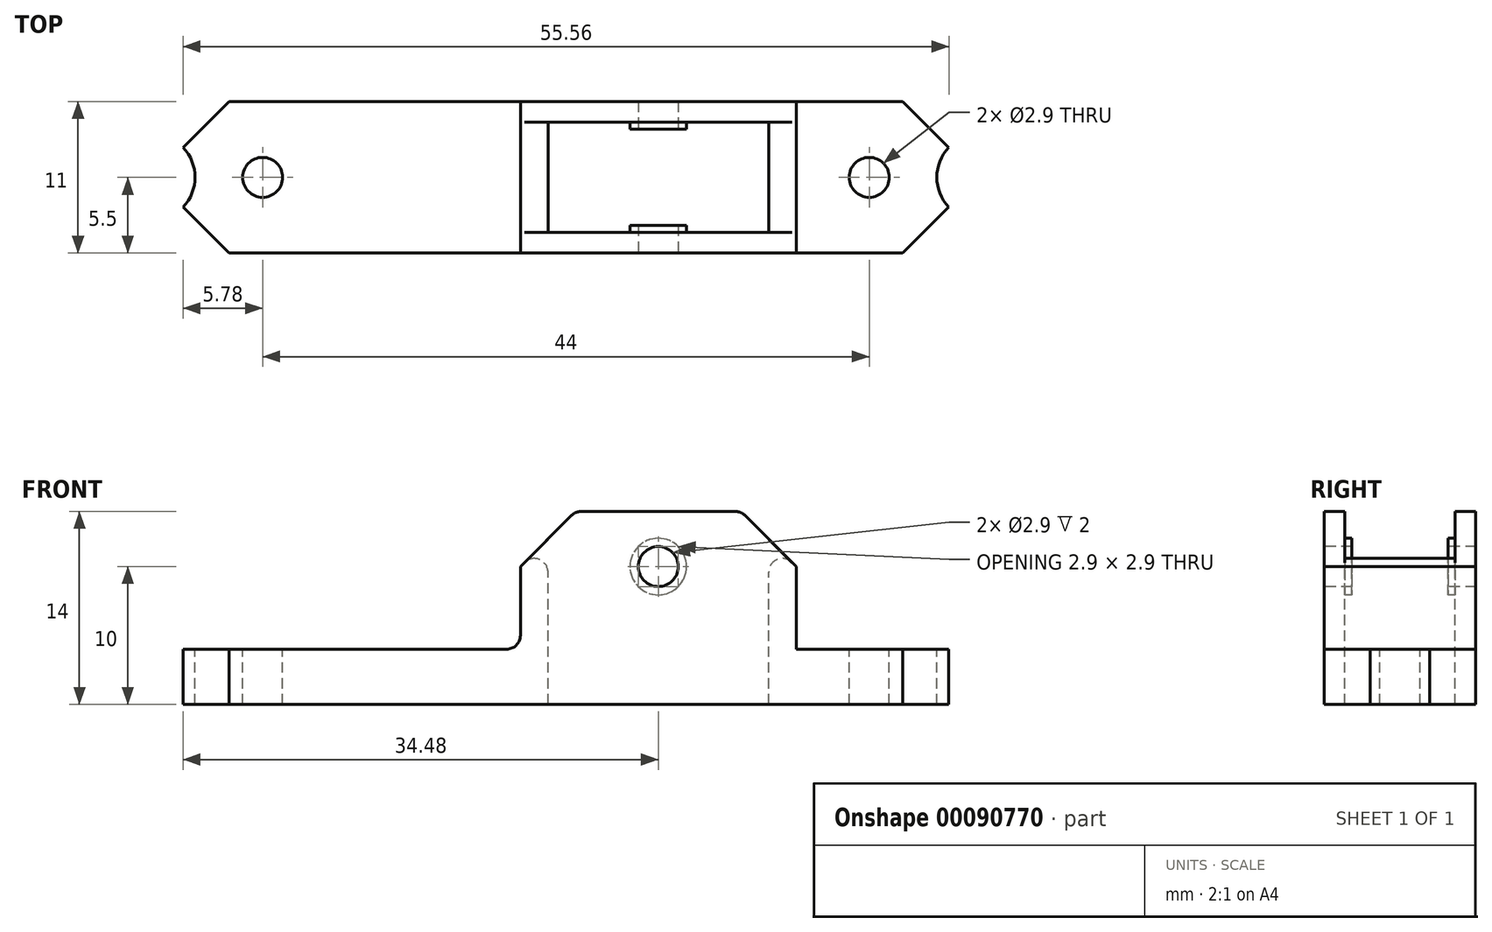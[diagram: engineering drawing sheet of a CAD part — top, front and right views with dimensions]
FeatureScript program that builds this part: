
annotation { "Feature Type Name" : "Feature", "Feature Type Description" : "" }
export const myFeature = defineFeature(function(context is Context, id is Id, definition is map)
    precondition{}
    {
        {
            var Q0;
            Q0=qCreatedBy(makeId("Top.planeOp"),FACE);
            var sketch = newSketch(context, id + "F0", { "sketchPlane" : qUnion([Q0])});
            skCircle(sketch, "E0", {"center": v(-30, 0) * mm, "radius": 3.1 * mm});
            skCircle(sketch, "E1", {"center": v(30, 0) * mm, "radius": 3.1 * mm});
            skLineSegment(sketch, "E2.bottom", {"start": v(-28.44, 5.5) * mm, "end": v(28.44, 5.5) * mm});
            skLineSegment(sketch, "E2.top", {"start": v(-28.44, -5.5) * mm, "end": v(28.44, -5.5) * mm});
            skLineSegment(sketch, "E2.left", {"start": v(-28.44, 5.5) * mm, "end": v(-28.44, -5.5) * mm});
            skLineSegment(sketch, "E2.right", {"start": v(28.44, 5.5) * mm, "end": v(28.44, -5.5) * mm});
            skPoint(sketch, "E2.middle", {"position": v(0, 0) * mm});
            skLineSegment(sketch, "E3.bottom", {"start": v(-1.3, 4) * mm, "end": v(14.7, 4) * mm});
            skLineSegment(sketch, "E3.top", {"start": v(-1.3, -4) * mm, "end": v(14.7, -4) * mm});
            skLineSegment(sketch, "E3.left", {"start": v(-1.3, 4) * mm, "end": v(-1.3, -4) * mm});
            skLineSegment(sketch, "E3.right", {"start": v(14.7, 4) * mm, "end": v(14.7, -4) * mm});
            skPoint(sketch, "E3.middle", {"position": v(6.7, 0) * mm});
            skLineSegment(sketch, "E4", {"start": v(-3.3, -5.5) * mm, "end": v(-3.3, 5.5) * mm});
            skLineSegment(sketch, "E5", {"start": v(16.7, -5.5) * mm, "end": v(16.7, 5.5) * mm});
            skCircle(sketch, "E6", {"center": v(-22, 0) * mm, "radius": 1.45 * mm});
            skPoint(sketch, "E6.centerSnap0", {"position": v(-28.44, 0) * mm});
            skCircle(sketch, "E7", {"center": v(22, 0) * mm, "radius": 1.45 * mm});
            skPoint(sketch, "E7.centerSnap0", {"position": v(28.44, 0) * mm});
            skLineSegment(sketch, "E8.bottom", {"start": v(4.2, 3.5) * mm, "end": v(9.2, 3.5) * mm});
            skLineSegment(sketch, "E8.top", {"start": v(4.2, -3.5) * mm, "end": v(9.2, -3.5) * mm});
            skLineSegment(sketch, "E8.left", {"start": v(4.2, 3.5) * mm, "end": v(4.2, -3.5) * mm});
            skLineSegment(sketch, "E8.right", {"start": v(9.2, 3.5) * mm, "end": v(9.2, -3.5) * mm});
            skSolve(sketch);
        }
        {
            var Q0;
            {var subQ7=sQuery(id+"F0.wireOp",EDGE,"E4");Q0=makeQuery(id+"F0.imprint","IMPRINT",FACE,{"disambiguationData":[TD([[makeQuery(id+"F0.imprint","IMPRINT",EDGE,{"derivedFrom":subQ7}),1.0]])]});}
            var Q1;
            {var subQ5=sQuery(id+"F0.wireOp",EDGE,"E5");Q1=makeQuery(id+"F0.imprint","IMPRINT",FACE,{"disambiguationData":[TD([[makeQuery(id+"F0.imprint","IMPRINT",EDGE,{"derivedFrom":subQ5}),-1.0]])]});}
            var Q2;
            Q2=makeQuery(id+"F0.imprint","IMPRINT",FACE,{"disambiguationData":[TD([[makeQuery(id+"F0.imprint","IMPRINT",EDGE,{"derivedFrom":sQuery(id+"F0.wireOp",EDGE,"E3.bottom")}),1.0]])]});
            extrude(context, id + "F1", {"entities" : qUnion([Q0, Q1, Q2]), "oppositeDirection" : true, "depth" : 4 * mm});
        }
        {
            var Q0;
            Q0=makeQuery(id+"F0.imprint","IMPRINT",FACE,{"disambiguationData":[TD([[makeQuery(id+"F0.imprint","IMPRINT",EDGE,{"derivedFrom":sQuery(id+"F0.wireOp",EDGE,"E3.bottom")}),1.0]])]});
            extrude(context, id + "F2", {"entities" : qUnion([Q0]), "operationType" : NewBodyOperationType.ADD, "depth" : 10 * mm});
        }
        {
            var Q0;
            {var subQ0=sQuery(id+"F0.wireOp",EDGE,"E2.top");Q0=makeQuery(id+"F2.boolean.opBoolean","MERGE",FACE,{"derivedFrom":[makeQuery(id+"F1.opExtrude","SWEPT_FACE",FACE,{"disambiguationData":[OSD([subQ0])]}),makeQuery(id+"F2.opExtrude","SWEPT_FACE",FACE,{"disambiguationData":[OSD([subQ0])]})]});}
            var sketch = newSketch(context, id + "F3", { "sketchPlane" : qUnion([Q0])});
            skCircle(sketch, "E9", {"center": v(6.7, 6) * mm, "radius": 1.45 * mm});
            skPoint(sketch, "E9.centerSnap0", {"position": v(6.7, 10) * mm});
            skCircle(sketch, "E10", {"center": v(6.7, 6) * mm, "radius": 2.05 * mm});
            skSolve(sketch);
        }
        {
            var Q0;
            Q0=makeQuery(id+"F3.imprint","IMPRINT",FACE,{"disambiguationData":[TD([[makeQuery(id+"F3.imprint","IMPRINT",EDGE,{"derivedFrom":sQuery(id+"F3.wireOp",EDGE,"E9")}),1.0]])]});
            extrude(context, id + "F4", {"entities" : qUnion([Q0]), "operationType" : NewBodyOperationType.REMOVE, "oppositeDirection" : true, "depth" : 25 * mm});
        }
        {
            var Q0;
            Q0=makeQuery(id+"F3.imprint","IMPRINT",FACE,{"disambiguationData":[TD([[makeQuery(id+"F3.imprint","IMPRINT",EDGE,{"derivedFrom":sQuery(id+"F3.wireOp",EDGE,"E9")}),-1.0]])]});
            var Q1;
            {var subQ0=sQuery(id+"F0.wireOp",EDGE,"E2.bottom");Q1=makeQuery(id+"F2.boolean.opBoolean","MERGE",FACE,{"derivedFrom":[makeQuery(id+"F1.opExtrude","SWEPT_FACE",FACE,{"disambiguationData":[OSD([subQ0])]}),makeQuery(id+"F2.opExtrude","SWEPT_FACE",FACE,{"disambiguationData":[OSD([subQ0])]})]});}
            extrude(context, id + "F5", {"entities" : qUnion([Q0]), "operationType" : NewBodyOperationType.ADD, "endBound" : BoundingType.UP_TO_SURFACE, "oppositeDirection" : true, "endBoundEntityFace" : qUnion([Q1]), "depth" : 25 * mm});
        }
        {
            var Q0;
            Q0=makeQuery(id+"F0.imprint","IMPRINT",FACE,{"disambiguationData":[TD([[makeQuery(id+"F0.imprint","IMPRINT",EDGE,{"derivedFrom":sQuery(id+"F0.wireOp",EDGE,"E8.bottom")}),-1.0]])]});
            extrude(context, id + "F6", {"entities" : qUnion([Q0]), "operationType" : NewBodyOperationType.REMOVE, "depth" : 25 * mm});
        }
        {
            var Q0;
            Q0=makeQuery(id+"F2.opExtrude","CAP_EDGE",EDGE,{"disambiguationData":[OSD([sQuery(id+"F0.wireOp",EDGE,"E4")])],"isStart":false});
            var Q1;
            Q1=makeQuery(id+"F2.opExtrude","CAP_EDGE",EDGE,{"disambiguationData":[OSD([sQuery(id+"F0.wireOp",EDGE,"E5")])],"isStart":false});
            var Q2;
            Q2=makeQuery(id+"F1.opExtrude","SWEPT_EDGE",EDGE,{"disambiguationData":[OSD([sQuery(id+"F0.wireOp",EDGE,"E2.top"),sQuery(id+"F0.wireOp",EDGE,"E2.left")])]});
            var Q3;
            Q3=makeQuery(id+"F1.opExtrude","SWEPT_EDGE",EDGE,{"disambiguationData":[OSD([sQuery(id+"F0.wireOp",EDGE,"E2.bottom"),sQuery(id+"F0.wireOp",EDGE,"E2.left")])]});
            var Q4;
            Q4=makeQuery(id+"F1.opExtrude","SWEPT_EDGE",EDGE,{"disambiguationData":[OSD([sQuery(id+"F0.wireOp",EDGE,"E2.top"),sQuery(id+"F0.wireOp",EDGE,"E2.right")])]});
            var Q5;
            Q5=makeQuery(id+"F1.opExtrude","SWEPT_EDGE",EDGE,{"disambiguationData":[OSD([sQuery(id+"F0.wireOp",EDGE,"E2.bottom"),sQuery(id+"F0.wireOp",EDGE,"E2.right")])]});
            chamfer(context, id + "F7", {"entities" : qUnion([Q0, Q1, Q2, Q3, Q4, Q5]), "width" : 4 * mm, "tangentPropagation" : true});
        }
        {
            var Q0;
            {var subQ0=sQuery(id+"F0.wireOp",EDGE,"E3.left");Q0=makeQuery(id+"F7.opChamfer","BLEND_EDGE",EDGE,{"blendedFrom":[makeQuery(id+"F2.opExtrude","CAP_EDGE",EDGE,{"disambiguationData":[OSD([sQuery(id+"F0.wireOp",EDGE,"E4")])],"isStart":false}),makeQuery(id+"F2.boolean.opBoolean","MERGE",FACE,{"derivedFrom":[makeQuery(id+"F1.opExtrude","SWEPT_FACE",FACE,{"disambiguationData":[OSD([subQ0])]}),makeQuery(id+"F2.opExtrude","SWEPT_FACE",FACE,{"disambiguationData":[OSD([subQ0])]})]})],"blendedInto":[makeQuery(id+"F2.boolean.opBoolean","MERGE",FACE,{"derivedFrom":[makeQuery(id+"F1.opExtrude","SWEPT_FACE",FACE,{"disambiguationData":[OSD([subQ0])]}),makeQuery(id+"F2.opExtrude","SWEPT_FACE",FACE,{"disambiguationData":[OSD([subQ0])]})]})]});}
            var Q1;
            {var subQ0=sQuery(id+"F0.wireOp",EDGE,"E3.right");Q1=makeQuery(id+"F7.opChamfer","BLEND_EDGE",EDGE,{"blendedFrom":[makeQuery(id+"F2.opExtrude","CAP_EDGE",EDGE,{"disambiguationData":[OSD([sQuery(id+"F0.wireOp",EDGE,"E5")])],"isStart":false}),makeQuery(id+"F2.boolean.opBoolean","MERGE",FACE,{"derivedFrom":[makeQuery(id+"F1.opExtrude","SWEPT_FACE",FACE,{"disambiguationData":[OSD([subQ0])]}),makeQuery(id+"F2.opExtrude","SWEPT_FACE",FACE,{"disambiguationData":[OSD([subQ0])]})]})],"blendedInto":[makeQuery(id+"F2.boolean.opBoolean","MERGE",FACE,{"derivedFrom":[makeQuery(id+"F1.opExtrude","SWEPT_FACE",FACE,{"disambiguationData":[OSD([subQ0])]}),makeQuery(id+"F2.opExtrude","SWEPT_FACE",FACE,{"disambiguationData":[OSD([subQ0])]})]})]});}
            var Q2;
            {var subQ0=sQuery(id+"F0.wireOp",EDGE,"E4");Q2=makeQuery(id+"F7.opChamfer","BLEND_EDGE",EDGE,{"disambiguationData":[OD(0.0)],"blendedFrom":[makeQuery(id+"F2.opExtrude","CAP_EDGE",EDGE,{"disambiguationData":[OSD([subQ0])],"isStart":false}),makeQuery(id+"F2.opExtrude","CAP_FACE",FACE,{"disambiguationData":[OSD([sQuery(id+"F0.wireOp",EDGE,"E2.bottom"),sQuery(id+"F0.wireOp",EDGE,"E2.top"),sQuery(id+"F0.wireOp",EDGE,"E3.bottom"),sQuery(id+"F0.wireOp",EDGE,"E3.top"),sQuery(id+"F0.wireOp",EDGE,"E3.left"),sQuery(id+"F0.wireOp",EDGE,"E3.right"),subQ0,sQuery(id+"F0.wireOp",EDGE,"E5")])],"isStart":false})],"blendedInto":[makeQuery(id+"F2.opExtrude","CAP_FACE",FACE,{"disambiguationData":[OSD([sQuery(id+"F0.wireOp",EDGE,"E2.bottom"),sQuery(id+"F0.wireOp",EDGE,"E2.top"),sQuery(id+"F0.wireOp",EDGE,"E3.bottom"),sQuery(id+"F0.wireOp",EDGE,"E3.top"),sQuery(id+"F0.wireOp",EDGE,"E3.left"),sQuery(id+"F0.wireOp",EDGE,"E3.right"),subQ0,sQuery(id+"F0.wireOp",EDGE,"E5")])],"isStart":false})]});}
            var Q3;
            {var subQ0=sQuery(id+"F0.wireOp",EDGE,"E5");Q3=makeQuery(id+"F7.opChamfer","BLEND_EDGE",EDGE,{"disambiguationData":[OD(1.0)],"blendedFrom":[makeQuery(id+"F2.opExtrude","CAP_EDGE",EDGE,{"disambiguationData":[OSD([subQ0])],"isStart":false}),makeQuery(id+"F2.opExtrude","CAP_FACE",FACE,{"disambiguationData":[OSD([sQuery(id+"F0.wireOp",EDGE,"E2.bottom"),sQuery(id+"F0.wireOp",EDGE,"E2.top"),sQuery(id+"F0.wireOp",EDGE,"E3.bottom"),sQuery(id+"F0.wireOp",EDGE,"E3.top"),sQuery(id+"F0.wireOp",EDGE,"E3.left"),sQuery(id+"F0.wireOp",EDGE,"E3.right"),sQuery(id+"F0.wireOp",EDGE,"E4"),subQ0])],"isStart":false})],"blendedInto":[makeQuery(id+"F2.opExtrude","CAP_FACE",FACE,{"disambiguationData":[OSD([sQuery(id+"F0.wireOp",EDGE,"E2.bottom"),sQuery(id+"F0.wireOp",EDGE,"E2.top"),sQuery(id+"F0.wireOp",EDGE,"E3.bottom"),sQuery(id+"F0.wireOp",EDGE,"E3.top"),sQuery(id+"F0.wireOp",EDGE,"E3.left"),sQuery(id+"F0.wireOp",EDGE,"E3.right"),sQuery(id+"F0.wireOp",EDGE,"E4"),subQ0])],"isStart":false})]});}
            var Q4;
            {var subQ0=sQuery(id+"F0.wireOp",EDGE,"E4");Q4=makeQuery(id+"F7.opChamfer","BLEND_EDGE",EDGE,{"disambiguationData":[OD(1.0)],"blendedFrom":[makeQuery(id+"F2.opExtrude","CAP_EDGE",EDGE,{"disambiguationData":[OSD([subQ0])],"isStart":false}),makeQuery(id+"F2.opExtrude","CAP_FACE",FACE,{"disambiguationData":[OSD([sQuery(id+"F0.wireOp",EDGE,"E2.bottom"),sQuery(id+"F0.wireOp",EDGE,"E2.top"),sQuery(id+"F0.wireOp",EDGE,"E3.bottom"),sQuery(id+"F0.wireOp",EDGE,"E3.top"),sQuery(id+"F0.wireOp",EDGE,"E3.left"),sQuery(id+"F0.wireOp",EDGE,"E3.right"),subQ0,sQuery(id+"F0.wireOp",EDGE,"E5")])],"isStart":false})],"blendedInto":[makeQuery(id+"F2.opExtrude","CAP_FACE",FACE,{"disambiguationData":[OSD([sQuery(id+"F0.wireOp",EDGE,"E2.bottom"),sQuery(id+"F0.wireOp",EDGE,"E2.top"),sQuery(id+"F0.wireOp",EDGE,"E3.bottom"),sQuery(id+"F0.wireOp",EDGE,"E3.top"),sQuery(id+"F0.wireOp",EDGE,"E3.left"),sQuery(id+"F0.wireOp",EDGE,"E3.right"),subQ0,sQuery(id+"F0.wireOp",EDGE,"E5")])],"isStart":false})]});}
            var Q5;
            {var subQ0=sQuery(id+"F0.wireOp",EDGE,"E5");Q5=makeQuery(id+"F7.opChamfer","BLEND_EDGE",EDGE,{"disambiguationData":[OD(0.0)],"blendedFrom":[makeQuery(id+"F2.opExtrude","CAP_EDGE",EDGE,{"disambiguationData":[OSD([subQ0])],"isStart":false}),makeQuery(id+"F2.opExtrude","CAP_FACE",FACE,{"disambiguationData":[OSD([sQuery(id+"F0.wireOp",EDGE,"E2.bottom"),sQuery(id+"F0.wireOp",EDGE,"E2.top"),sQuery(id+"F0.wireOp",EDGE,"E3.bottom"),sQuery(id+"F0.wireOp",EDGE,"E3.top"),sQuery(id+"F0.wireOp",EDGE,"E3.left"),sQuery(id+"F0.wireOp",EDGE,"E3.right"),sQuery(id+"F0.wireOp",EDGE,"E4"),subQ0])],"isStart":false})],"blendedInto":[makeQuery(id+"F2.opExtrude","CAP_FACE",FACE,{"disambiguationData":[OSD([sQuery(id+"F0.wireOp",EDGE,"E2.bottom"),sQuery(id+"F0.wireOp",EDGE,"E2.top"),sQuery(id+"F0.wireOp",EDGE,"E3.bottom"),sQuery(id+"F0.wireOp",EDGE,"E3.top"),sQuery(id+"F0.wireOp",EDGE,"E3.left"),sQuery(id+"F0.wireOp",EDGE,"E3.right"),sQuery(id+"F0.wireOp",EDGE,"E4"),subQ0])],"isStart":false})]});}
            var Q6;
            Q6=makeQuery(id+"F2.opExtrude","CAP_EDGE",EDGE,{"disambiguationData":[OSD([sQuery(id+"F0.wireOp",EDGE,"E4")])],"isStart":true});
            var Q7;
            Q7=makeQuery(id+"F2.opExtrude","CAP_EDGE",EDGE,{"disambiguationData":[OSD([sQuery(id+"F0.wireOp",EDGE,"E5")])],"isStart":true});
            fillet(context, id + "F8", {"entities" : qUnion([Q0, Q1, Q2, Q3, Q4, Q5, Q6, Q7]), "radius" : 1 * mm, "tangentPropagation" : true, "allowEdgeOverflow" : false});
        }
    });
